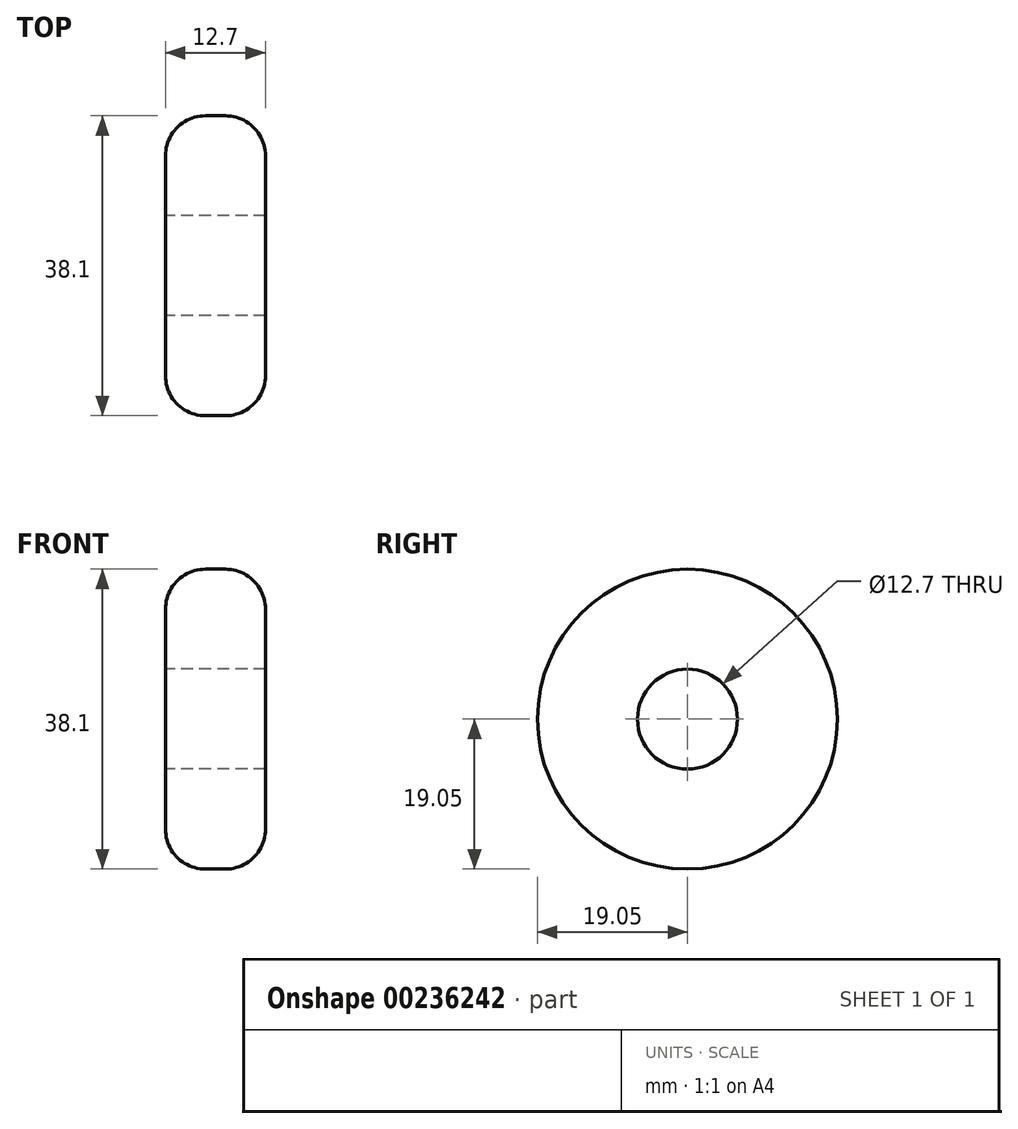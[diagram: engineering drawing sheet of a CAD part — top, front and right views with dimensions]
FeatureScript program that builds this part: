
annotation { "Feature Type Name" : "Feature", "Feature Type Description" : "" }
export const myFeature = defineFeature(function(context is Context, id is Id, definition is map)
    precondition{}
    {
        {
            var Q0;
            Q0=qCreatedBy(makeId("Right.planeOp"),FACE);
            var sketch = newSketch(context, id + "F0", { "sketchPlane" : qUnion([Q0])});
            skCircle(sketch, "E0", {"center": v(0, 0) * mm, "radius": 19.05 * mm});
            skCircle(sketch, "E1", {"center": v(0, 0) * mm, "radius": 6.35 * mm});
            skSolve(sketch);
        }
        {
            var Q0;
            Q0 = qSketchRegion(id + "F0", true);
            extrude(context, id + "F1", {"entities" : qUnion([Q0]), "endBound" : BoundingType.SYMMETRIC, "depth" : 12.7 * mm});
        }
        {
            var Q0;
            Q0=makeQuery(id+"F1.opExtrude","CAP_EDGE",EDGE,{"disambiguationData":[OSD([sQuery(id+"F0.wireOp",EDGE,"E0")])],"isStart":false});
            fillet(context, id + "F2", {"entities" : qUnion([Q0]), "radius" : 5.08 * mm, "tangentPropagation" : true, "allowEdgeOverflow" : false});
        }
        {
            var Q0;
            Q0=makeQuery(id+"F1.opExtrude","SWEPT_FACE",FACE,{"disambiguationData":[OSD([sQuery(id+"F0.wireOp",EDGE,"E0")])]});
            fillet(context, id + "F3", {"entities" : qUnion([Q0]), "radius" : 5.08 * mm, "tangentPropagation" : true, "allowEdgeOverflow" : false});
        }
    });
